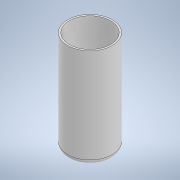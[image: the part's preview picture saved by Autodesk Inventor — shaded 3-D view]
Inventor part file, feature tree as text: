
AUTODESK INVENTOR PART (.ipt)
format: ipt  version: 2020 (Build 240168000, 168)  size: 120,832 bytes
history: native  units: mm
features: revolve x1, sketch x1
ambient origin geometry x8: Origin, YZ Plane, XZ Plane, XY Plane, X Axis, Y Axis, Z Axis, Center Point
bodies: Solid1 (feature_tree)
feature tree (2):
  revolve  "Revolution1"  [1 undecoded]
  sketch  "Sketch1"  dims[d0=90.0mm d1=200.0mm d2=10.0mm d5=3.5mm d6=3.5mm d7=90.0deg]
note: 1 required parameter value undecoded (feature->parameter linkage not recoverable at this tier; creation-order binding heuristic only, values carry confidence <= 0.55)
